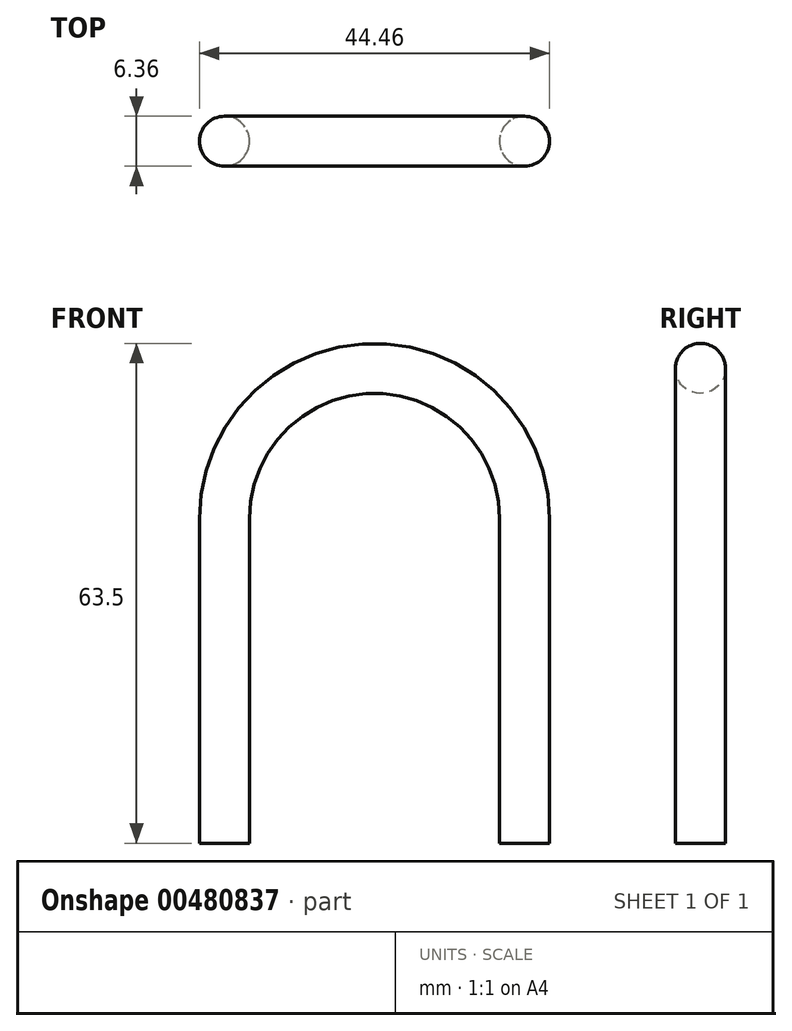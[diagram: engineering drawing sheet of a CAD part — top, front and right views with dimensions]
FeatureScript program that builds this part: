
annotation { "Feature Type Name" : "Feature", "Feature Type Description" : "" }
export const myFeature = defineFeature(function(context is Context, id is Id, definition is map)
    precondition{}
    {
        {
            var Q0;
            Q0=qCreatedBy(makeId("Front.planeOp"),FACE);
            var sketch = newSketch(context, id + "F0", { "sketchPlane" : qUnion([Q0])});
            skLineSegment(sketch, "E0", {"start": v(19.05, 0) * mm, "end": v(19.05, 41.27) * mm});
            skArc(sketch, "E1", {"start": v(19.05, 41.28) * mm, "mid": v(0, 60.33) * mm, "end": v(-19.05, 41.28) * mm});
            skLineSegment(sketch, "E2", {"start": v(-19.05, 41.27) * mm, "end": v(-19.05, 0) * mm});
            skSolve(sketch);
        }
        {
            var Q0;
            Q0=qCreatedBy(makeId("Top.planeOp"),FACE);
            var sketch = newSketch(context, id + "F1", { "sketchPlane" : qUnion([Q0])});
            skCircle(sketch, "E3", {"center": v(19.05, 0) * mm, "radius": 3.17 * mm});
            skSolve(sketch);
        }
        {
            var Q0;
            Q0=makeQuery(id+"F1.imprint","IMPRINT",FACE,{"disambiguationData":[TD([[makeQuery(id+"F1.imprint","IMPRINT",EDGE,{"derivedFrom":sQuery(id+"F1.wireOp",EDGE,"E3")}),1.0]])]});
            var Q1;
            Q1=qBodyType(qCreatedBy(id+"F0",EDGE),BodyType.WIRE);
            sweep(context, id + "F2", {"profiles" : qUnion([Q0]), "path" : qUnion([Q1])});
        }
    });
